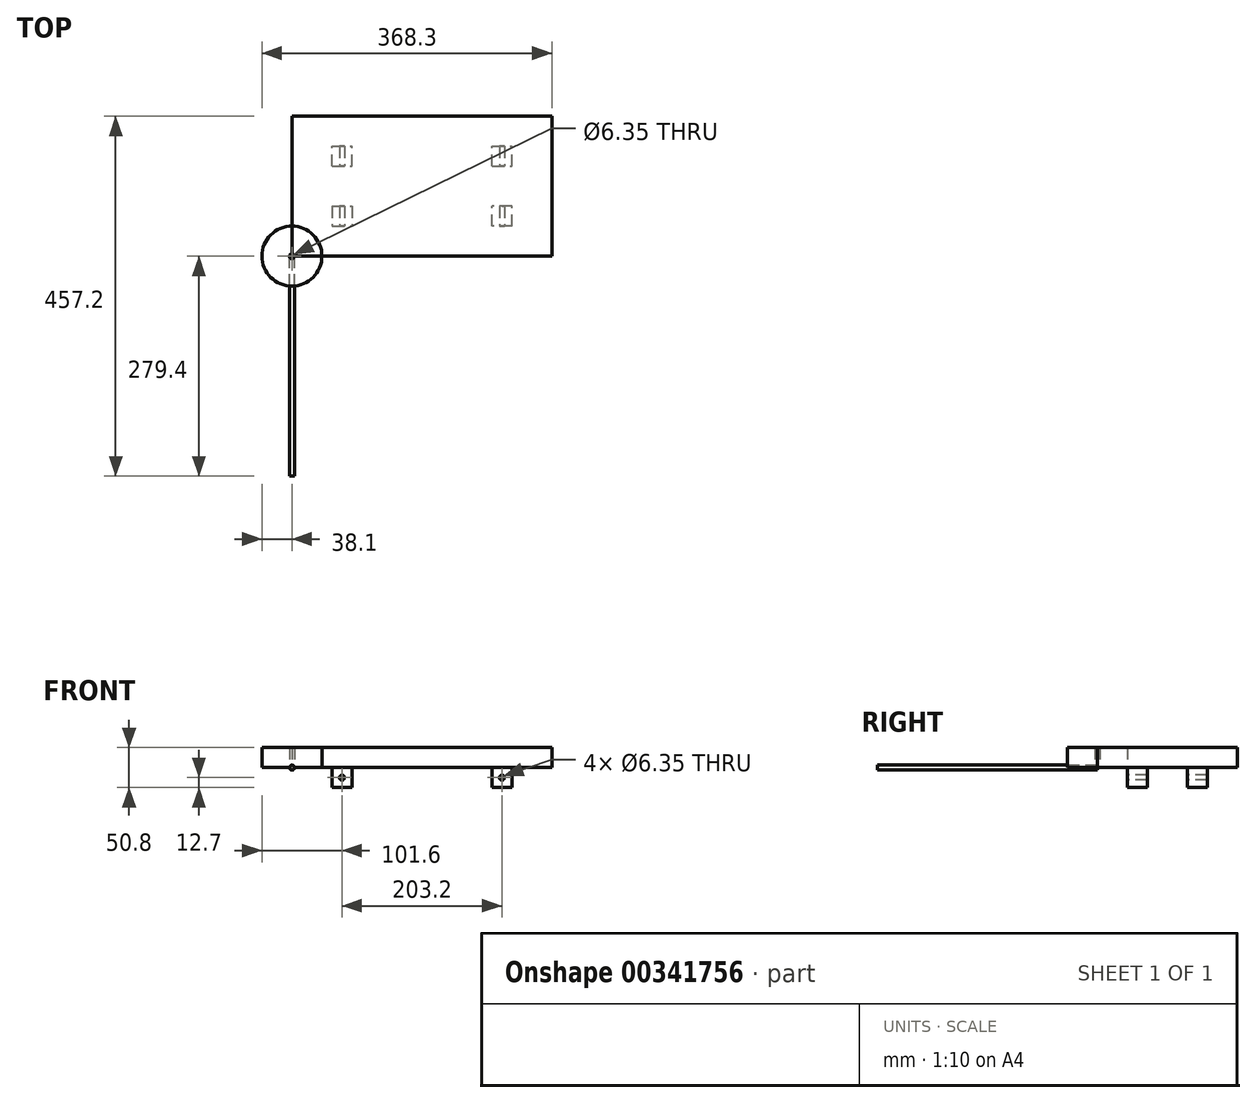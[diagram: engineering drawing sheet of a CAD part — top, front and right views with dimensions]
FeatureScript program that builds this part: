
annotation { "Feature Type Name" : "Feature", "Feature Type Description" : "" }
export const myFeature = defineFeature(function(context is Context, id is Id, definition is map)
    precondition{}
    {
        {
            var Q0;
            Q0=qCreatedBy(makeId("Top.planeOp"),FACE);
            var sketch = newSketch(context, id + "F0", { "sketchPlane" : qUnion([Q0])});
            skLineSegment(sketch, "E0.bottom", {"start": v(0, 0) * mm, "end": v(330.2, 0) * mm});
            skLineSegment(sketch, "E0.top", {"start": v(0, 177.8) * mm, "end": v(330.2, 177.8) * mm});
            skLineSegment(sketch, "E0.left", {"start": v(0, 0) * mm, "end": v(0, 177.8) * mm});
            skLineSegment(sketch, "E0.right", {"start": v(330.2, 0) * mm, "end": v(330.2, 177.8) * mm});
            skSolve(sketch);
        }
        {
            var Q0;
            Q0=makeQuery(id+"F0.imprint","IMPRINT",FACE,{"disambiguationData":[TD([[makeQuery(id+"F0.imprint","IMPRINT",EDGE,{"derivedFrom":sQuery(id+"F0.wireOp",EDGE,"E0.bottom")}),1.0]])]});
            extrude(context, id + "F1", {"entities" : qUnion([Q0]), "depth" : 25.4 * mm});
        }
        {
            var Q0;
            Q0=qCreatedBy(makeId("Top.planeOp"),FACE);
            var sketch = newSketch(context, id + "F2", { "sketchPlane" : qUnion([Q0])});
            skCircle(sketch, "E1", {"center": v(0, 0) * mm, "radius": 38.1 * mm});
            skCircle(sketch, "E2", {"center": v(0, 0) * mm, "radius": 3.18 * mm});
            skSolve(sketch);
        }
        {
            var Q0;
            Q0=makeQuery(id+"F2.imprint","IMPRINT",FACE,{"disambiguationData":[TD([[makeQuery(id+"F2.imprint","IMPRINT",EDGE,{"derivedFrom":sQuery(id+"F2.wireOp",EDGE,"E1")}),1.0]])]});
            extrude(context, id + "F3", {"entities" : qUnion([Q0]), "depth" : 25.4 * mm});
        }
        {
            var Q0;
            Q0=qCreatedBy(makeId("Front.planeOp"),FACE);
            var sketch = newSketch(context, id + "F4", { "sketchPlane" : qUnion([Q0])});
            skCircle(sketch, "E3", {"center": v(0, 0) * mm, "radius": 3.17 * mm});
            skSolve(sketch);
        }
        {
            var Q0;
            Q0 = qSketchRegion(id + "F4", true);
            extrude(context, id + "F5", {"entities" : qUnion([Q0]), "depth" : 279.4 * mm});
        }
        {
            var Q0;
            Q0=qCreatedBy(makeId("Top.planeOp"),FACE);
            var sketch = newSketch(context, id + "F6", { "sketchPlane" : qUnion([Q0])});
            skLineSegment(sketch, "E4.bottom", {"start": v(50.8, 114.3) * mm, "end": v(76.2, 114.3) * mm});
            skLineSegment(sketch, "E4.top", {"start": v(50.8, 139.7) * mm, "end": v(76.2, 139.7) * mm});
            skLineSegment(sketch, "E4.left", {"start": v(50.8, 114.3) * mm, "end": v(50.8, 139.7) * mm});
            skLineSegment(sketch, "E4.right", {"start": v(76.2, 114.3) * mm, "end": v(76.2, 139.7) * mm});
            skLineSegment(sketch, "E5.bottom", {"start": v(50.8, 63.5) * mm, "end": v(76.2, 63.5) * mm});
            skLineSegment(sketch, "E5.top", {"start": v(50.8, 38.1) * mm, "end": v(76.2, 38.1) * mm});
            skLineSegment(sketch, "E5.left", {"start": v(50.8, 63.5) * mm, "end": v(50.8, 38.1) * mm});
            skLineSegment(sketch, "E5.right", {"start": v(76.2, 63.5) * mm, "end": v(76.2, 38.1) * mm});
            skLineSegment(sketch, "E6.bottom", {"start": v(254, 114.3) * mm, "end": v(279.4, 114.3) * mm});
            skLineSegment(sketch, "E6.top", {"start": v(254, 139.7) * mm, "end": v(279.4, 139.7) * mm});
            skLineSegment(sketch, "E6.left", {"start": v(254, 114.3) * mm, "end": v(254, 139.7) * mm});
            skLineSegment(sketch, "E6.right", {"start": v(279.4, 114.3) * mm, "end": v(279.4, 139.7) * mm});
            skPoint(sketch, "E7.firstSnap0", {"position": v(279.4, 127) * mm});
            skLineSegment(sketch, "E7.bottom", {"start": v(279.4, 38.1) * mm, "end": v(254, 38.1) * mm});
            skLineSegment(sketch, "E7.top", {"start": v(279.4, 63.5) * mm, "end": v(254, 63.5) * mm});
            skLineSegment(sketch, "E7.left", {"start": v(279.4, 38.1) * mm, "end": v(279.4, 63.5) * mm});
            skLineSegment(sketch, "E7.right", {"start": v(254, 38.1) * mm, "end": v(254, 63.5) * mm});
            skSolve(sketch);
        }
        {
            var Q0;
            Q0=makeQuery(id+"F6.imprint","IMPRINT",FACE,{"disambiguationData":[TD([[makeQuery(id+"F6.imprint","IMPRINT",EDGE,{"derivedFrom":sQuery(id+"F6.wireOp",EDGE,"E5.bottom")}),-1.0]])]});
            var Q1;
            Q1=makeQuery(id+"F6.imprint","IMPRINT",FACE,{"disambiguationData":[TD([[makeQuery(id+"F6.imprint","IMPRINT",EDGE,{"derivedFrom":sQuery(id+"F6.wireOp",EDGE,"E4.bottom")}),1.0]])]});
            var Q2;
            Q2=makeQuery(id+"F6.imprint","IMPRINT",FACE,{"disambiguationData":[TD([[makeQuery(id+"F6.imprint","IMPRINT",EDGE,{"derivedFrom":sQuery(id+"F6.wireOp",EDGE,"E6.bottom")}),1.0]])]});
            var Q3;
            Q3=makeQuery(id+"F6.imprint","IMPRINT",FACE,{"disambiguationData":[TD([[makeQuery(id+"F6.imprint","IMPRINT",EDGE,{"derivedFrom":sQuery(id+"F6.wireOp",EDGE,"E7.bottom")}),-1.0]])]});
            extrude(context, id + "F7", {"entities" : qUnion([Q0, Q1, Q2, Q3]), "operationType" : NewBodyOperationType.ADD, "oppositeDirection" : true, "depth" : 25.4 * mm});
        }
        {
            var Q0;
            Q0=makeQuery(id+"F7.opExtrude","SWEPT_FACE",FACE,{"disambiguationData":[OSD([sQuery(id+"F6.wireOp",EDGE,"E5.top")])]});
            var sketch = newSketch(context, id + "F8", { "sketchPlane" : qUnion([Q0])});
            skCircle(sketch, "E8", {"center": v(63.5, -12.7) * mm, "radius": 3.17 * mm});
            skPoint(sketch, "E8.centerSnap0", {"position": v(63.5, -25.4) * mm});
            skCircle(sketch, "E9", {"center": v(266.7, -12.7) * mm, "radius": 3.17 * mm});
            skSolve(sketch);
        }
        {
            var Q0;
            Q0 = qSketchRegion(id + "F8", true);
            extrude(context, id + "F9", {"entities" : qUnion([Q0]), "operationType" : NewBodyOperationType.REMOVE, "endBound" : BoundingType.THROUGH_ALL, "oppositeDirection" : true, "depth" : 25.4 * mm});
        }
    });
